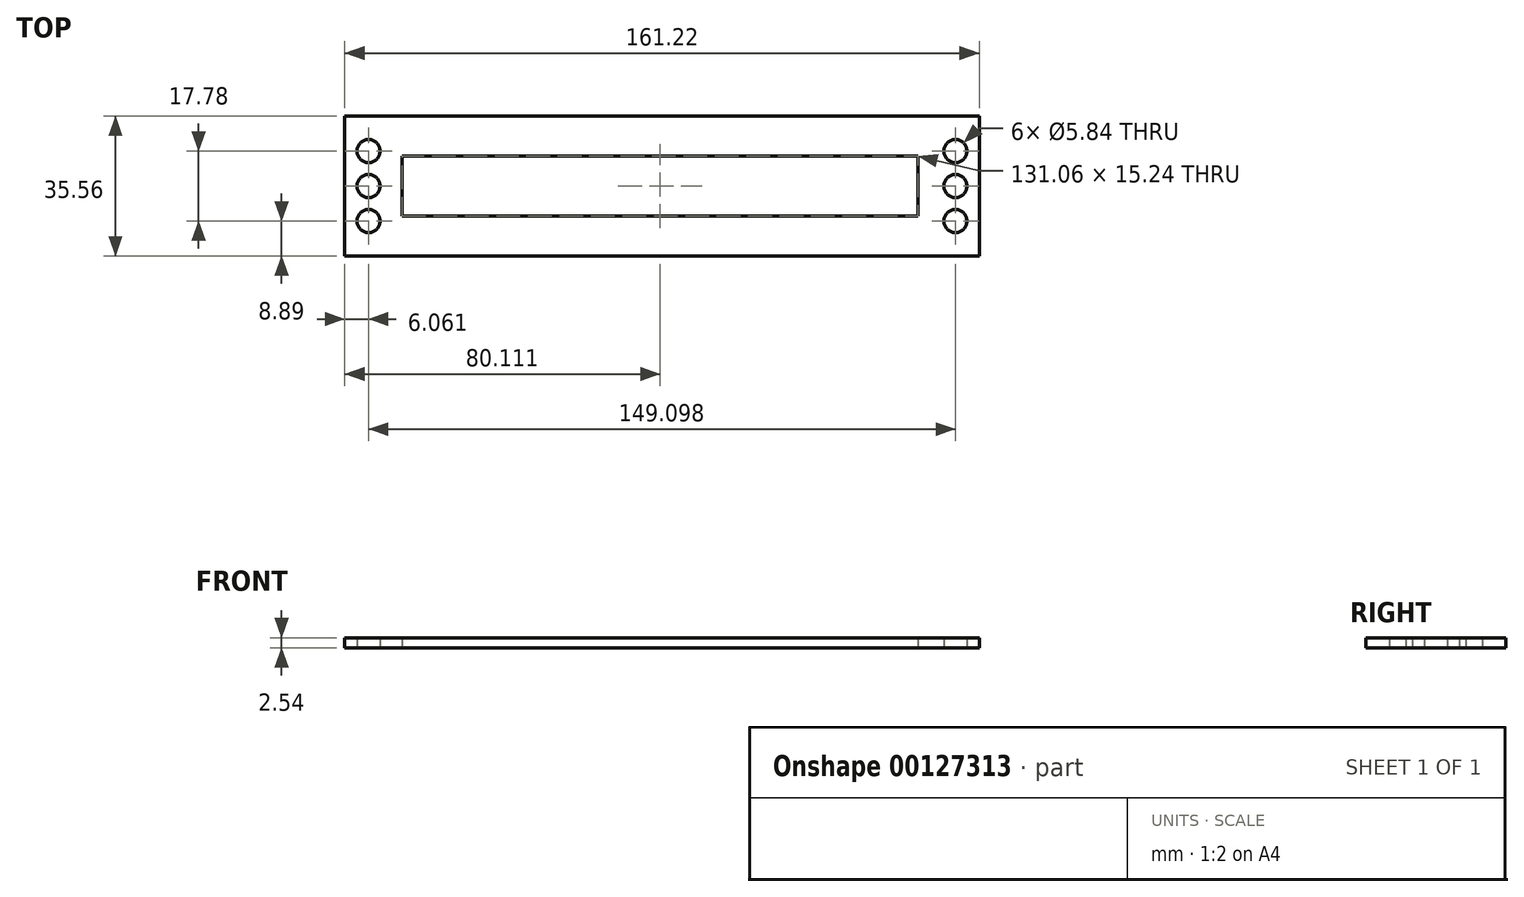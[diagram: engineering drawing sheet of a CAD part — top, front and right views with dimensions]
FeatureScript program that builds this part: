
annotation { "Feature Type Name" : "Feature", "Feature Type Description" : "" }
export const myFeature = defineFeature(function(context is Context, id is Id, definition is map)
    precondition{}
    {
        {
            var Q0;
            Q0=qCreatedBy(makeId("Top.planeOp"),FACE);
            var sketch = newSketch(context, id + "F0", { "sketchPlane" : qUnion([Q0])});
            skLineSegment(sketch, "E0.bottom", {"start": v(80.6, 17.78) * mm, "end": v(-80.6, 17.78) * mm});
            skLineSegment(sketch, "E0.top", {"start": v(80.6, -17.78) * mm, "end": v(-80.6, -17.78) * mm});
            skLineSegment(sketch, "E0.left", {"start": v(80.6, 17.78) * mm, "end": v(80.6, -17.78) * mm});
            skLineSegment(sketch, "E0.right", {"start": v(-80.6, 17.78) * mm, "end": v(-80.6, -17.78) * mm});
            skPoint(sketch, "E0.middle", {"position": v(0, 0) * mm});
            skLineSegment(sketch, "E1.bottom", {"start": v(68.5, 17.78) * mm, "end": v(-68.5, 17.78) * mm});
            skLineSegment(sketch, "E1.top", {"start": v(68.5, -17.78) * mm, "end": v(-68.5, -17.78) * mm});
            skLineSegment(sketch, "E2.bottom", {"start": v(-66.03, 7.62) * mm, "end": v(65.03, 7.62) * mm});
            skLineSegment(sketch, "E2.top", {"start": v(-66.03, -7.62) * mm, "end": v(65.03, -7.62) * mm});
            skLineSegment(sketch, "E2.left", {"start": v(-66.03, 7.62) * mm, "end": v(-66.03, -7.62) * mm});
            skLineSegment(sketch, "E2.right", {"start": v(65.03, 7.62) * mm, "end": v(65.03, -7.62) * mm});
            skCircle(sketch, "E3", {"center": v(-74.55, 8.89) * mm, "radius": 2.92 * mm});
            skCircle(sketch, "E4", {"center": v(-74.55, 0) * mm, "radius": 2.92 * mm});
            skCircle(sketch, "E5", {"center": v(-74.55, -8.9) * mm, "radius": 2.92 * mm});
            skCircle(sketch, "E6.MirrorC", {"center": v(74.55, -8.9) * mm, "radius": 2.92 * mm});
            skCircle(sketch, "E7.MirrorC", {"center": v(74.55, 0) * mm, "radius": 2.92 * mm});
            skCircle(sketch, "E8.MirrorC", {"center": v(74.55, 8.89) * mm, "radius": 2.92 * mm});
            skSolve(sketch);
        }
        {
            var Q0;
            Q0 = qSketchRegion(id + "F0", true);
            extrude(context, id + "F1", {"entities" : qUnion([Q0]), "endBound" : BoundingType.SYMMETRIC, "depth" : 2.54 * mm});
        }
    });
